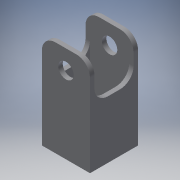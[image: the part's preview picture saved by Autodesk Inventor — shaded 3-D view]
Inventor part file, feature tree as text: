
AUTODESK INVENTOR PART (.ipt)
format: ipt  version: 2018.2 (Build 222227000, 227)  size: 145,920 bytes
history: native  units: mm
features: extrude x3, sketch x3, other x1, shell x1, fillet x1
ambient origin geometry x8: Origin, YZ Plane, XZ Plane, XY Plane, X Axis, Y Axis, Z Axis, Center Point
bodies: Body1 (feature_tree)
feature tree (9):
  other  "ソリッド1"
  extrude  "押し出し1"  Depth=25.0mm
  shell  "シェル1"  Thickness=25.0mm
  extrude  "押し出し2"  Depth=50.0mm TaperAngle=0.0deg
  extrude  "押し出し3"  Depth=2.3mm
  fillet  "フィレット1"  Radius=20.0mm
  sketch  "スケッチ1"
  sketch  "スケッチ2"
  sketch  "スケッチ3"
